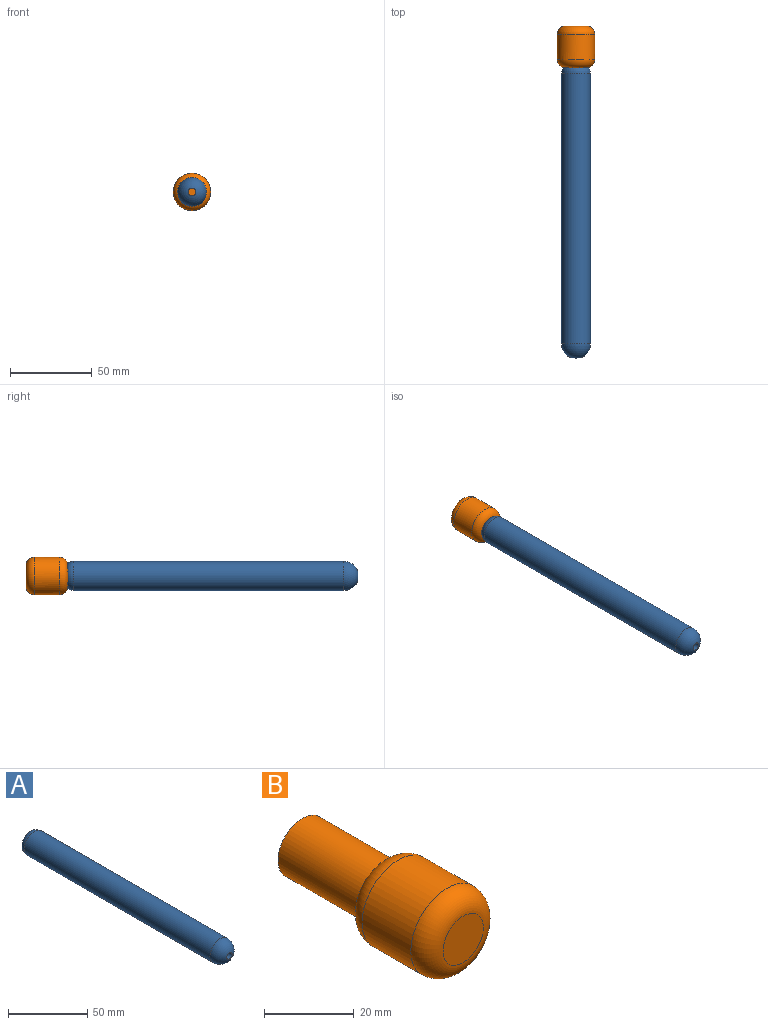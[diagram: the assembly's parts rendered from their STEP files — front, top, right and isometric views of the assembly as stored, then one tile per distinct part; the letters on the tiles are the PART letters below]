
ASSEMBLY  parts=2 mates=1
PART A: 6 faces, bbox 17.8x177.5x17.8 mm
  f0: cylinder r=8.89mm len=165.55mm, axis (0,1,0), area 9247.2mm2, adj f1,f5
  f1: sphere r=8.89mm, area 477.9mm2, adj f0,f4
  f2: cylinder r=7.62mm len=169.09mm, axis (0,1,0), area 8095.6mm2, adj f3,f5
  f3: plane 15.24x15.24mm, normal (0,1,0), area 164.1mm2, adj f2,f4
  f4: cylinder r=2.41mm len=8.38mm, axis (0,1,0), area 127mm2, adj f1,f3
  f5: torus R=3.81mm, axis (0,1,0), area 195.1mm2, adj f0,f2
PART B: 6 faces, bbox 24.7x50.8x24.7 mm
  f0: cylinder r=7.62mm len=25.4mm, axis (0,1,0), area 1216.1mm2, adj f1,f4
  f1: plane 15.24x15.24mm, normal (0,1,0), area 182.4mm2, adj f0
  f2: cylinder r=11.43mm len=22.86mm, axis (0,1,0), area 1106.1mm2, adj f4,f5
  f3: plane 12.7x12.7mm, normal (0,-1,0), area 126.7mm2, adj f5
  f4: torus R=6.35mm, axis (0,1,0), area 424.2mm2, adj f0,f2
  f5: torus R=6.35mm, axis (0,-1,0), area 480.5mm2, adj f2,f3
PLACE A t=(-0.11,12.51,0.06)mm
PLACE B rot(axis=(1,0,0),180deg) t=(-0.11,63.31,0.06)mm
MATE fastened B.f0 <-> A.f2  axis (0,-1,0) through (-0.11,88.71,0.06)mm
